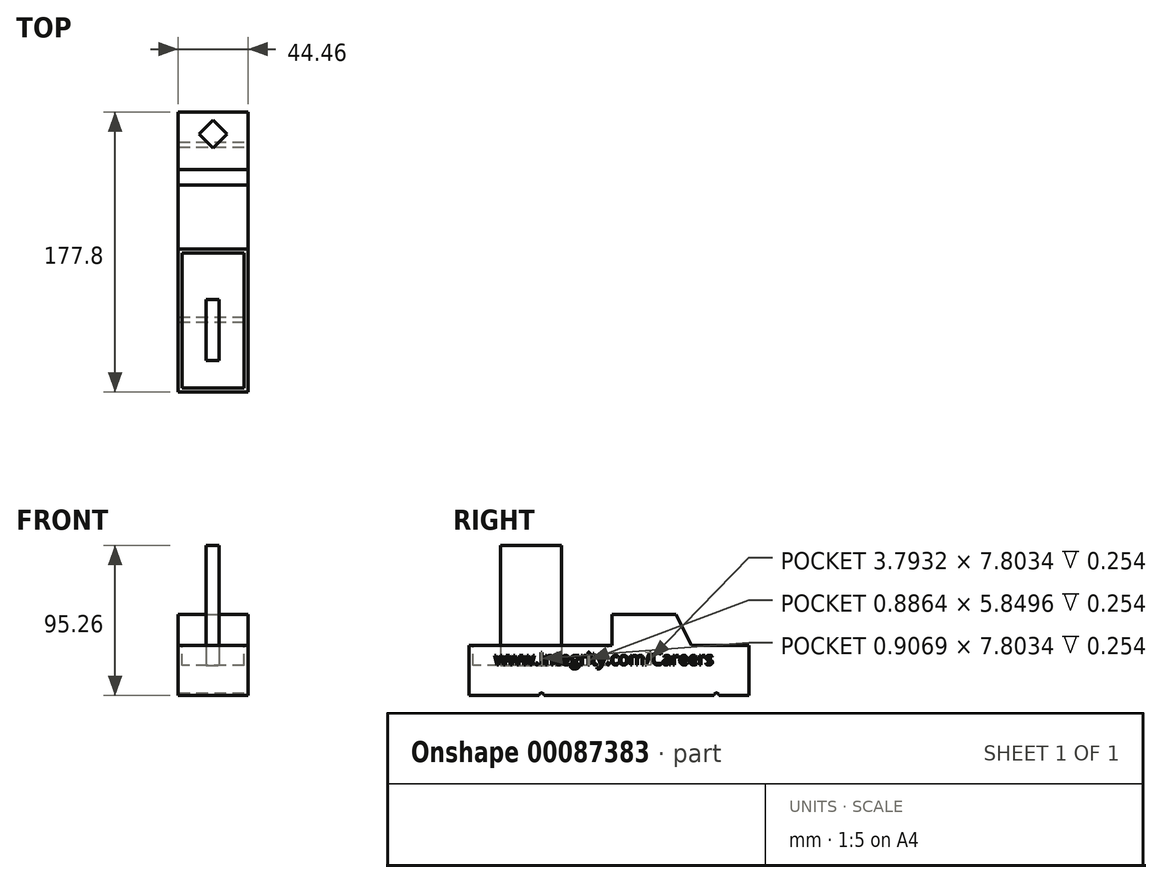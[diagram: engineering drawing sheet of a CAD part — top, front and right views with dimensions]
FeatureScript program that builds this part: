
annotation { "Feature Type Name" : "Feature", "Feature Type Description" : "" }
export const myFeature = defineFeature(function(context is Context, id is Id, definition is map)
    precondition{}
    {
        {
            var Q0;
            Q0=qCreatedBy(makeId("Front.planeOp"),FACE);
            var sketch = newSketch(context, id + "F0", { "sketchPlane" : qUnion([Q0])});
            skLineSegment(sketch, "E0.bottom", {"start": v(22.22, 15.88) * mm, "end": v(-22.23, 15.88) * mm});
            skLineSegment(sketch, "E0.top", {"start": v(22.23, -15.88) * mm, "end": v(-22.22, -15.88) * mm});
            skLineSegment(sketch, "E0.left", {"start": v(22.22, 15.88) * mm, "end": v(22.23, -15.88) * mm});
            skLineSegment(sketch, "E0.right", {"start": v(-22.23, 15.88) * mm, "end": v(-22.22, -15.88) * mm});
            skPoint(sketch, "E0.middle", {"position": v(0, 0) * mm});
            skSolve(sketch);
        }
        {
            var Q0;
            Q0=makeQuery(id+"F0.imprint","IMPRINT",FACE,{"disambiguationData":[TD([[makeQuery(id+"F0.imprint","IMPRINT",EDGE,{"derivedFrom":sQuery(id+"F0.wireOp",EDGE,"E0.bottom")}),1.0]])]});
            extrude(context, id + "F1", {"entities" : qUnion([Q0]), "oppositeDirection" : true, "depth" : 177.8 * mm});
        }
        {
            var Q0;
            Q0=makeQuery(id+"F1.opExtrude","SWEPT_FACE",FACE,{"disambiguationData":[OSD([sQuery(id+"F0.wireOp",EDGE,"E0.left")])]});
            var sketch = newSketch(context, id + "F2", { "sketchPlane" : qUnion([Q0])});
            skLineSegment(sketch, "E1.bottom", {"start": v(44.45, -15.88) * mm, "end": v(47.62, -15.88) * mm});
            skLineSegment(sketch, "E2.bottom", {"start": v(155.57, -15.88) * mm, "end": v(158.75, -15.88) * mm});
            skArc(sketch, "E3", {"start": v(47.62, -15.88) * mm, "mid": v(46.04, -14.29) * mm, "end": v(44.45, -15.88) * mm});
            skArc(sketch, "E4", {"start": v(158.75, -15.88) * mm, "mid": v(157.16, -14.29) * mm, "end": v(155.57, -15.88) * mm});
            skSolve(sketch);
        }
        {
            var Q0;
            Q0=makeQuery(id+"F2.imprint","IMPRINT",FACE,{"disambiguationData":[TD([[makeQuery(id+"F2.imprint","IMPRINT",EDGE,{"derivedFrom":sQuery(id+"F2.wireOp",EDGE,"E1.bottom")}),-1.0]])]});
            var Q1;
            Q1=makeQuery(id+"F2.imprint","IMPRINT",FACE,{"disambiguationData":[TD([[makeQuery(id+"F2.imprint","IMPRINT",EDGE,{"derivedFrom":sQuery(id+"F2.wireOp",EDGE,"E2.bottom")}),-1.0]])]});
            extrude(context, id + "F3", {"entities" : qUnion([Q0, Q1]), "operationType" : NewBodyOperationType.REMOVE, "endBound" : BoundingType.THROUGH_ALL, "oppositeDirection" : true, "depth" : 25.4 * mm});
        }
        {
            var Q0;
            Q0=makeQuery(id+"F1.opExtrude","SWEPT_FACE",FACE,{"disambiguationData":[OSD([sQuery(id+"F0.wireOp",EDGE,"E0.bottom")])]});
            var sketch = newSketch(context, id + "F4", { "sketchPlane" : qUnion([Q0])});
            skLineSegment(sketch, "E5.bottom", {"start": v(19.69, 88.14) * mm, "end": v(-19.69, 88.14) * mm});
            skLineSegment(sketch, "E5.top", {"start": v(19.69, 2.54) * mm, "end": v(-19.69, 2.54) * mm});
            skLineSegment(sketch, "E5.left", {"start": v(19.69, 88.14) * mm, "end": v(19.69, 2.54) * mm});
            skLineSegment(sketch, "E5.right", {"start": v(-19.69, 88.14) * mm, "end": v(-19.69, 2.54) * mm});
            skPoint(sketch, "E5.middle", {"position": v(0, 45.34) * mm});
            skLineSegment(sketch, "E6.0", {"start": v(-22.23, 177.8) * mm, "end": v(-22.23, 0) * mm});
            skLineSegment(sketch, "E7.0", {"start": v(22.22, 177.8) * mm, "end": v(22.22, 0) * mm});
            skLineSegment(sketch, "E8.0", {"start": v(22.22, 0) * mm, "end": v(-22.23, 0) * mm});
            skSolve(sketch);
        }
        {
            var Q0;
            Q0=makeQuery(id+"F4.imprint","IMPRINT",FACE,{"disambiguationData":[TD([[makeQuery(id+"F4.imprint","IMPRINT",EDGE,{"derivedFrom":sQuery(id+"F4.wireOp",EDGE,"E5.bottom")}),1.0]])]});
            extrude(context, id + "F5", {"entities" : qUnion([Q0]), "operationType" : NewBodyOperationType.REMOVE, "oppositeDirection" : true, "depth" : 12.7 * mm});
        }
        {
            var Q0;
            Q0=makeQuery(id+"F1.opExtrude","SWEPT_FACE",FACE,{"disambiguationData":[OSD([sQuery(id+"F0.wireOp",EDGE,"E0.bottom")])]});
            var sketch = newSketch(context, id + "F6", { "sketchPlane" : qUnion([Q0])});
            skLineSegment(sketch, "E9", {"start": v(0, 172.76) * mm, "end": v(-8.85, 163.91) * mm});
            skLineSegment(sketch, "E10", {"start": v(-8.85, 163.91) * mm, "end": v(0, 155.07) * mm});
            skLineSegment(sketch, "E11", {"start": v(0, 155.07) * mm, "end": v(8.85, 163.91) * mm});
            skLineSegment(sketch, "E12", {"start": v(8.85, 163.91) * mm, "end": v(0, 172.76) * mm});
            skPoint(sketch, "E13", {"position": v(0, 88.14) * mm});
            skLineSegment(sketch, "E14", {"start": v(0, 172.76) * mm, "end": v(0, 155.07) * mm, "construction": true});
            skSolve(sketch);
        }
        {
            var Q0;
            Q0=makeQuery(id+"F6.imprint","IMPRINT",FACE,{"disambiguationData":[TD([[makeQuery(id+"F6.imprint","IMPRINT",EDGE,{"derivedFrom":sQuery(id+"F6.wireOp",EDGE,"E9")}),1.0]])]});
            extrude(context, id + "F7", {"entities" : qUnion([Q0]), "operationType" : NewBodyOperationType.ADD, "depth" : 0.05 * mm});
        }
        {
            var Q0;
            Q0=makeQuery(id+"F1.opExtrude","SWEPT_FACE",FACE,{"disambiguationData":[OSD([sQuery(id+"F0.wireOp",EDGE,"E0.left")])]});
            var sketch = newSketch(context, id + "F8", { "sketchPlane" : qUnion([Q0])});
            skText(sketch, "E15", { "text": "www.Integrity.com/Careers", "fontName": "OpenSans-Regular.ttf"});
            const initialGuessF8  = {"E15": [0.0161, 0.00363, 1, 0, 0.00787]};
            skSetInitialGuess(sketch, initialGuessF8);
            skSolve(sketch);
        }
        {
            var Q0;
            Q0 = qSketchRegion(id + "F8", true);
            extrude(context, id + "F9", {"entities" : qUnion([Q0]), "operationType" : NewBodyOperationType.REMOVE, "oppositeDirection" : true, "depth" : 0.25 * mm});
        }
        {
            var Q0;
            Q0=makeQuery(id+"F5.boolean.opBoolean","COPY",FACE,{"derivedFrom":makeQuery(id+"F5.opExtrude","CAP_FACE",FACE,{"disambiguationData":[OSD([sQuery(id+"F4.wireOp",EDGE,"E5.bottom"),sQuery(id+"F4.wireOp",EDGE,"E5.top"),sQuery(id+"F4.wireOp",EDGE,"E5.left"),sQuery(id+"F4.wireOp",EDGE,"E5.right")])],"isStart":false})});
            var sketch = newSketch(context, id + "F10", { "sketchPlane" : qUnion([Q0])});
            skLineSegment(sketch, "E16.bottom", {"start": v(-4.31, 20.09) * mm, "end": v(3.71, 20.09) * mm});
            skLineSegment(sketch, "E16.top", {"start": v(-4.31, 58.85) * mm, "end": v(3.71, 58.85) * mm});
            skLineSegment(sketch, "E16.left", {"start": v(-4.31, 20.09) * mm, "end": v(-4.31, 58.85) * mm});
            skLineSegment(sketch, "E16.right", {"start": v(3.71, 20.09) * mm, "end": v(3.71, 58.85) * mm});
            skSolve(sketch);
        }
        {
            var Q0;
            Q0=makeQuery(id+"F10.imprint","IMPRINT",FACE,{"disambiguationData":[TD([[makeQuery(id+"F10.imprint","IMPRINT",EDGE,{"derivedFrom":sQuery(id+"F10.wireOp",EDGE,"E16.bottom")}),1.0]])]});
            extrude(context, id + "F11", {"entities" : qUnion([Q0]), "operationType" : NewBodyOperationType.ADD, "depth" : 76.2 * mm});
        }
        {
            var Q0;
            Q0=qCreatedBy(makeId("Right.planeOp"),FACE);
            var sketch = newSketch(context, id + "F12", { "sketchPlane" : qUnion([Q0])});
            skLineSegment(sketch, "E17.0", {"start": v(177.8, 15.88) * mm, "end": v(0, 15.88) * mm});
            skLineSegment(sketch, "E18", {"start": v(90.68, 15.88) * mm, "end": v(90.68, 35.74) * mm});
            skLineSegment(sketch, "E19", {"start": v(90.68, 35.74) * mm, "end": v(131.3, 35.74) * mm});
            skLineSegment(sketch, "E20", {"start": v(131.3, 35.74) * mm, "end": v(141.4, 15.88) * mm});
            skLineSegment(sketch, "E21.0.1", {"start": v(88.14, 15.87) * mm, "end": v(88.14, 3.18) * mm});
            skLineSegment(sketch, "E21.0.3", {"start": v(88.14, 3.18) * mm, "end": v(88.14, 15.88) * mm});
            skSolve(sketch);
        }
        {
            var Q0;
            {var subQ0=sQuery(id+"F12.wireOp",EDGE,"E18");Q0=makeQuery(id+"F12.imprint","IMPRINT",FACE,{"disambiguationData":[TD([[makeQuery(id+"F12.imprint","IMPRINT",EDGE,{"derivedFrom":subQ0}),-1.0]])]});}
            var Q1;
            {var subQ1=sQuery(id+"F0.wireOp",EDGE,"E0.left");var subQ3=sQuery(id+"F0.wireOp",EDGE,"E0.bottom");Q1=makeQuery(id+"F9.boolean.opBoolean","SPLIT",FACE,{"disambiguationData":[TD([makeQuery(id+"F1.opExtrude","SWEPT_FACE",FACE,{"disambiguationData":[OSD([subQ3])]})])],"derivedFrom":makeQuery(id+"F1.opExtrude","SWEPT_FACE",FACE,{"disambiguationData":[OSD([subQ1])]})});}
            var Q2;
            Q2=makeQuery(id+"F1.opExtrude","SWEPT_FACE",FACE,{"disambiguationData":[OSD([sQuery(id+"F0.wireOp",EDGE,"E0.right")])]});
            extrude(context, id + "F13", {"entities" : qUnion([Q0]), "operationType" : NewBodyOperationType.ADD, "endBound" : BoundingType.SYMMETRIC, "oppositeDirection" : true, "endBoundEntityFace" : qUnion([Q1]), "depth" : 44.45 * mm, "hasSecondDirection" : true, "secondDirectionBound" : SecondDirectionBoundingType.UP_TO_SURFACE, "secondDirectionOppositeDirection" : false, "secondDirectionBoundEntityFace" : qUnion([Q2]), "secondDirectionDepth" : 25.4 * mm});
        }
    });
